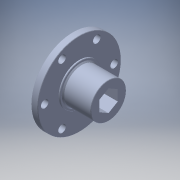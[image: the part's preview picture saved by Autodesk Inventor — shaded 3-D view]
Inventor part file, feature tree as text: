
AUTODESK INVENTOR PART (.ipt)
format: ipt  version: 2016 (Build 200138000, 138)  size: 173,056 bytes
history: native  units: in
note: dims shown in document units (in); Inventor stores cm internally (conversion verified against a paired STEP export)
features: chamfer x1
ambient origin geometry x8: Origin, YZ Plane, XZ Plane, XY Plane, X Axis, Y Axis, Z Axis, Center Point
bodies: Solid1 (feature_tree)
feature tree (1):
  chamfer  "Chamfer3"  [1 undecoded]
note: 1 required parameter value undecoded (feature->parameter linkage not recoverable at this tier; creation-order binding heuristic only, values carry confidence <= 0.55)
